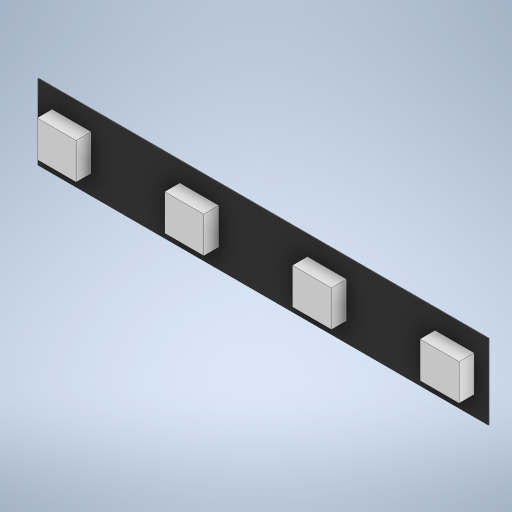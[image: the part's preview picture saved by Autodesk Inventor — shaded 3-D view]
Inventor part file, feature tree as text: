
AUTODESK INVENTOR PART (.ipt)
format: ipt  version: 2023 (Build 270158000, 158)  size: 282,112 bytes
history: native  units: mm
features: extrude x2, sketch x2, other x1
ambient origin geometry x8: Origin, YZ Plane, XZ Plane, XY Plane, X Axis, Y Axis, Z Axis, Center Point
bodies: Body1 (feature_tree)
feature tree (5):
  other  "솔리드1"
  extrude  "돌출1"  Depth=60.0mm
  extrude  "돌출2"  Depth=10.0mm
  sketch  "스케치1"
  sketch  "스케치2"
